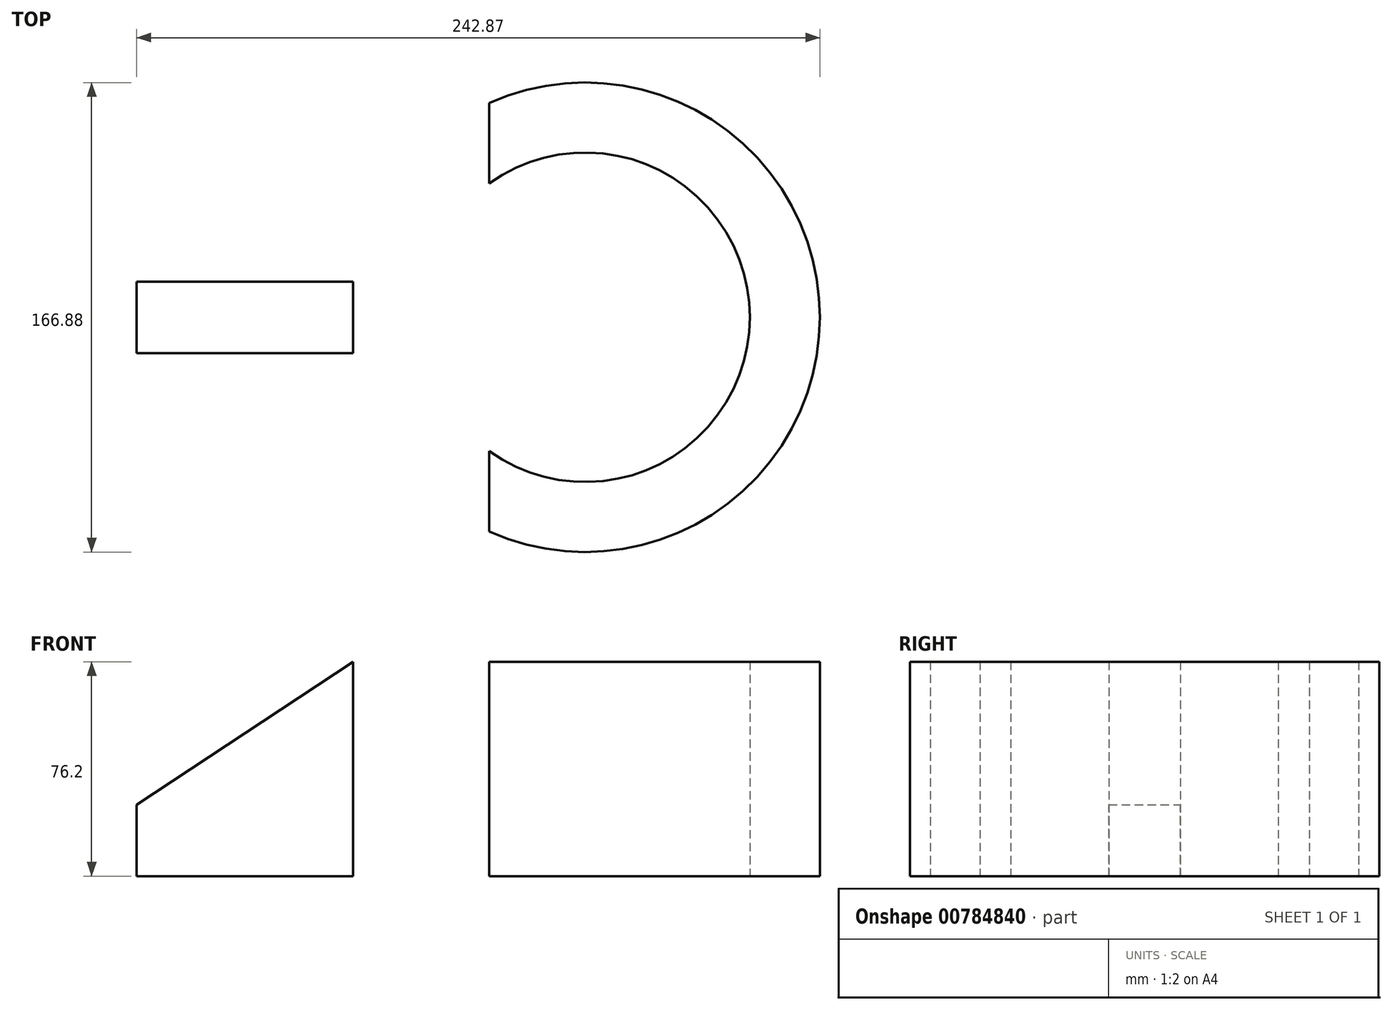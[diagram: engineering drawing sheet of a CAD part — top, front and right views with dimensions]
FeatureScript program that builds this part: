
annotation { "Feature Type Name" : "Feature", "Feature Type Description" : "" }
export const myFeature = defineFeature(function(context is Context, id is Id, definition is map)
    precondition{}
    {
        {
            var Q0;
            Q0=qCreatedBy(makeId("Top.planeOp"),FACE);
            var sketch = newSketch(context, id + "F0", { "sketchPlane" : qUnion([Q0])});
            skLineSegment(sketch, "E0.bottom", {"start": v(76.23, -76.14) * mm, "end": v(-76.16, -76.14) * mm});
            skLineSegment(sketch, "E0.top", {"start": v(76.23, 76.15) * mm, "end": v(-76.16, 76.15) * mm});
            skLineSegment(sketch, "E0.left", {"start": v(76.23, -76.14) * mm, "end": v(76.23, 76.15) * mm});
            skLineSegment(sketch, "E0.right", {"start": v(-76.16, -76.14) * mm, "end": v(-76.16, 76.15) * mm});
            skSolve(sketch);
        }
        {
            var Q0;
            Q0 = qSketchRegion(id + "F0", true);
            extrude(context, id + "F1", {"entities" : qUnion([Q0]), "depth" : 25.4 * mm, "offsetDistance" : 25.4 * mm});
        }
        {
            var Q0;
            Q0=makeQuery(id+"F1.opExtrude","CAP_FACE",FACE,{"disambiguationData":[OSD([sQuery(id+"F0.wireOp",EDGE,"E0.bottom"),sQuery(id+"F0.wireOp",EDGE,"E0.top"),sQuery(id+"F0.wireOp",EDGE,"E0.left"),sQuery(id+"F0.wireOp",EDGE,"E0.right")])],"isStart":false});
            var sketch = newSketch(context, id + "F2", { "sketchPlane" : qUnion([Q0])});
            skLineSegment(sketch, "E1", {"start": v(-49.09, 0) * mm, "end": v(-49.09, 12.7) * mm});
            skLineSegment(sketch, "E2", {"start": v(-49.09, 0) * mm, "end": v(-49.09, -12.7) * mm});
            skLineSegment(sketch, "E3", {"start": v(-49.09, 12.7) * mm, "end": v(27.88, 12.7) * mm});
            skLineSegment(sketch, "E4", {"start": v(27.88, 12.7) * mm, "end": v(27.88, -12.7) * mm});
            skLineSegment(sketch, "E5", {"start": v(27.88, -12.7) * mm, "end": v(-49.09, -12.7) * mm});
            skSolve(sketch);
        }
        {
            var Q0;
            Q0=makeQuery(id+"F2.imprint","IMPRINT",FACE,{"disambiguationData":[TD([[makeQuery(id+"F2.imprint","IMPRINT",EDGE,{"derivedFrom":sQuery(id+"F2.wireOp",EDGE,"E1")}),-1.0]])]});
            extrude(context, id + "F3", {"entities" : qUnion([Q0]), "operationType" : NewBodyOperationType.ADD, "depth" : 50.8 * mm, "offsetDistance" : 25.4 * mm});
        }
        {
            var Q0;
            Q0=makeQuery(id+"F3.opExtrude","SWEPT_FACE",FACE,{"disambiguationData":[OSD([sQuery(id+"F2.wireOp",EDGE,"E5")])]});
            var sketch = newSketch(context, id + "F4", { "sketchPlane" : qUnion([Q0])});
            skLineSegment(sketch, "E6", {"start": v(27.88, 76.2) * mm, "end": v(-49.09, 25.4) * mm});
            skSolve(sketch);
        }
        {
            var Q0;
            Q0=makeQuery(id+"F4.imprint","IMPRINT",FACE,{"disambiguationData":[TD([[makeQuery(id+"F4.imprint","IMPRINT",EDGE,{"derivedFrom":sQuery(id+"F4.wireOp",EDGE,"E6")}),-1.0]])]});
            extrude(context, id + "F5", {"entities" : qUnion([Q0]), "operationType" : NewBodyOperationType.REMOVE, "oppositeDirection" : true, "depth" : 25.4 * mm, "offsetDistance" : 25.4 * mm});
        }
        {
            var Q0;
            Q0=makeQuery(id+"F1.opExtrude","CAP_FACE",FACE,{"disambiguationData":[OSD([sQuery(id+"F0.wireOp",EDGE,"E0.bottom"),sQuery(id+"F0.wireOp",EDGE,"E0.top"),sQuery(id+"F0.wireOp",EDGE,"E0.left"),sQuery(id+"F0.wireOp",EDGE,"E0.right")])],"isStart":false});
            var sketch = newSketch(context, id + "F6", { "sketchPlane" : qUnion([Q0])});
            skArc(sketch, "E7", {"start": v(76.23, 76.15) * mm, "mid": v(26.9, 0) * mm, "end": v(76.23, -76.14) * mm});
            skCircle(sketch, "E8", {"center": v(110.34, 0) * mm, "radius": 83.44 * mm});
            skCircle(sketch, "E9", {"center": v(110.34, 0) * mm, "radius": 58.55 * mm});
            skSolve(sketch);
        }
        {
            var Q0;
            {var subQ0=makeQuery(id+"F3.opExtrude","CAP_EDGE",EDGE,{"disambiguationData":[OSD([sQuery(id+"F2.wireOp",EDGE,"E4")])],"isStart":true});Q0=makeQuery(id+"F6.imprint","IMPRINT",FACE,{"disambiguationData":[TD([[makeQuery(id+"F6.imprint","IMPRINT",EDGE,{"derivedFrom":subQ0}),1.0]])]});}
            var Q1;
            {var subQ1=makeQuery(id+"F1.opExtrude","CAP_EDGE",EDGE,{"disambiguationData":[OSD([sQuery(id+"F0.wireOp",EDGE,"E0.left")])],"isStart":false});var subQ4=sQuery(id+"F6.wireOp",EDGE,"E9");var subQ6=makeQuery(id+"F6.imprint","INTERSECT",VERTEX,{"disambiguationData":[OD(0.0)],"derivedFrom":[subQ1,subQ4]});Q1=makeQuery(id+"F6.imprint","IMPRINT",FACE,{"disambiguationData":[TD([[makeQuery(id+"F6.imprint","IMPRINT",EDGE,{"disambiguationData":[TD([[subQ6,-1.0]])],"derivedFrom":subQ4}),-1.0]])]});}
            extrude(context, id + "F7", {"entities" : qUnion([Q0, Q1]), "operationType" : NewBodyOperationType.ADD, "depth" : 50.8 * mm, "offsetDistance" : 25.4 * mm});
        }
        {
            var Q0;
            Q0=makeQuery(id+"F7.opExtrude","CAP_FACE",FACE,{"disambiguationData":[OSD([sQuery(id+"F2.wireOp",EDGE,"E3"),sQuery(id+"F2.wireOp",EDGE,"E4"),sQuery(id+"F6.wireOp",EDGE,"E8"),sQuery(id+"F6.wireOp",EDGE,"E9")])],"isStart":true});
            extrude(context, id + "F8", {"entities" : qUnion([Q0]), "operationType" : NewBodyOperationType.ADD, "depth" : 25.4 * mm, "offsetDistance" : 25.4 * mm});
        }
        {
            var Q0;
            {var subQ0=sQuery(id+"F0.wireOp",EDGE,"E0.left");var subQ1=sQuery(id+"F6.wireOp",EDGE,"E9");Q0=makeQuery(id+"F7.boolean.opBoolean","SPLIT",FACE,{"disambiguationData":[TD([makeQuery(id+"F7.opExtrude","SWEPT_FACE",FACE,{"disambiguationData":[OSD([subQ1])]})])],"derivedFrom":makeQuery(id+"F1.opExtrude","CAP_FACE",FACE,{"disambiguationData":[OSD([sQuery(id+"F0.wireOp",EDGE,"E0.bottom"),sQuery(id+"F0.wireOp",EDGE,"E0.top"),subQ0,sQuery(id+"F0.wireOp",EDGE,"E0.right")])],"isStart":false})});}
            extrude(context, id + "F9", {"entities" : qUnion([Q0]), "operationType" : NewBodyOperationType.REMOVE, "oppositeDirection" : true, "depth" : 68.07 * mm, "offsetDistance" : 25.4 * mm});
        }
    });
